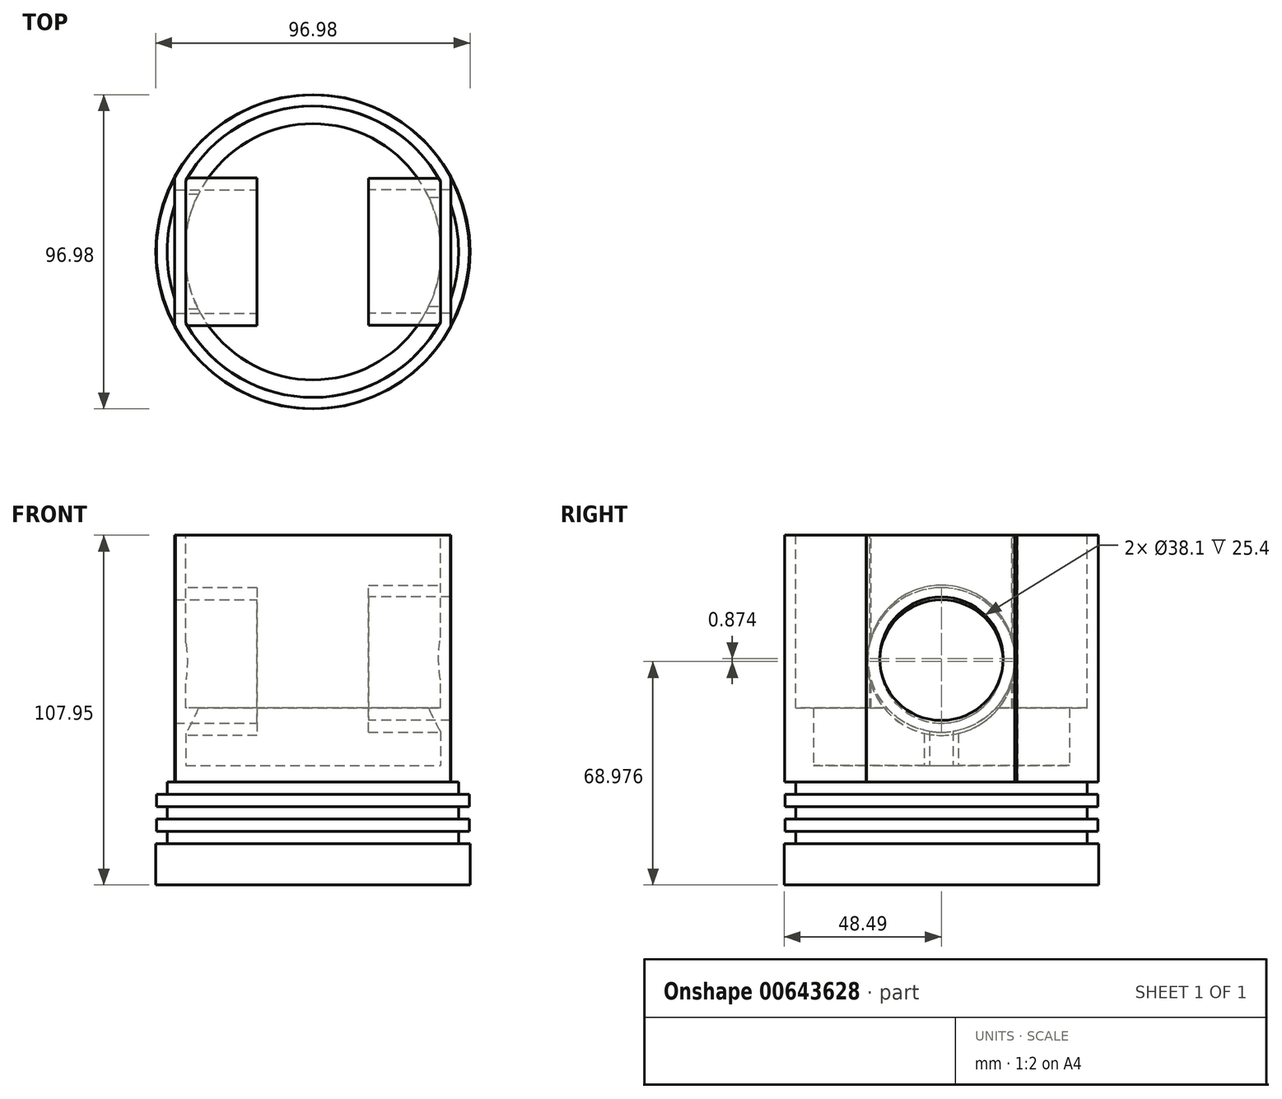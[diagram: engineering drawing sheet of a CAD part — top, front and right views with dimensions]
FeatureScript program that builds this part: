
annotation { "Feature Type Name" : "Feature", "Feature Type Description" : "" }
export const myFeature = defineFeature(function(context is Context, id is Id, definition is map)
    precondition{}
    {
        {
            var Q0;
            Q0=qCreatedBy(makeId("Top.planeOp"),FACE);
            var sketch = newSketch(context, id + "F0", { "sketchPlane" : qUnion([Q0])});
            skCircle(sketch, "E0", {"center": v(0, 0) * mm, "radius": 48.42 * mm});
            skSolve(sketch);
        }
        {
            var Q0;
            Q0=makeQuery(id+"F0.imprint","IMPRINT",FACE,{"disambiguationData":[TD([[makeQuery(id+"F0.imprint","IMPRINT",EDGE,{"derivedFrom":sQuery(id+"F0.wireOp",EDGE,"E0")}),1.0]])]});
            extrude(context, id + "F1", {"entities" : qUnion([Q0]), "depth" : 76.2 * mm, "offsetDistance" : 25.4 * mm});
        }
        {
            var Q0;
            Q0=makeQuery(id+"F1.opExtrude","CAP_FACE",FACE,{"disambiguationData":[OSD([sQuery(id+"F0.wireOp",EDGE,"E0")])],"isStart":false});
            var sketch = newSketch(context, id + "F2", { "sketchPlane" : qUnion([Q0])});
            skCircle(sketch, "E1", {"center": v(0, 0) * mm, "radius": 44.96 * mm});
            skSolve(sketch);
        }
        {
            var Q0;
            Q0=makeQuery(id+"F2.imprint","IMPRINT",FACE,{"disambiguationData":[TD([[makeQuery(id+"F2.imprint","IMPRINT",EDGE,{"derivedFrom":sQuery(id+"F2.wireOp",EDGE,"E1")}),1.0]])]});
            extrude(context, id + "F3", {"entities" : qUnion([Q0]), "operationType" : NewBodyOperationType.REMOVE, "oppositeDirection" : true, "depth" : 71.12 * mm, "offsetDistance" : 25.4 * mm});
        }
        {
            var Q0;
            Q0=qCreatedBy(makeId("Top.planeOp"),FACE);
            var sketch = newSketch(context, id + "F4", { "sketchPlane" : qUnion([Q0])});
            skCircle(sketch, "E2", {"center": v(0, 0) * mm, "radius": 44.96 * mm});
            skSolve(sketch);
        }
        {
            var Q0;
            Q0=makeQuery(id+"F4.imprint","IMPRINT",FACE,{"disambiguationData":[TD([[makeQuery(id+"F4.imprint","IMPRINT",EDGE,{"derivedFrom":sQuery(id+"F4.wireOp",EDGE,"E2")}),1.0]])]});
            extrude(context, id + "F5", {"entities" : qUnion([Q0]), "operationType" : NewBodyOperationType.ADD, "oppositeDirection" : true, "depth" : 3.8 * mm, "offsetDistance" : 25.4 * mm});
        }
        {
            var Q0;
            Q0=makeQuery(id+"F5.opExtrude","CAP_FACE",FACE,{"disambiguationData":[OSD([sQuery(id+"F4.wireOp",EDGE,"E2")])],"isStart":false});
            var sketch = newSketch(context, id + "F6", { "sketchPlane" : qUnion([Q0])});
            skCircle(sketch, "E3", {"center": v(0, 0) * mm, "radius": 48.26 * mm});
            skSolve(sketch);
        }
        {
            var Q0;
            Q0 = qSketchRegion(id + "F6", true);
            extrude(context, id + "F7", {"entities" : qUnion([Q0]), "operationType" : NewBodyOperationType.ADD, "depth" : 3.8 * mm, "offsetDistance" : 25.4 * mm});
        }
        {
            var Q0;
            Q0=makeQuery(id+"F7.opExtrude","CAP_FACE",FACE,{"disambiguationData":[OSD([sQuery(id+"F6.wireOp",EDGE,"E3")])],"isStart":false});
            var sketch = newSketch(context, id + "F8", { "sketchPlane" : qUnion([Q0])});
            skCircle(sketch, "E4", {"center": v(0, 0) * mm, "radius": 44.96 * mm});
            skSolve(sketch);
        }
        {
            var Q0;
            Q0=makeQuery(id+"F8.imprint","IMPRINT",FACE,{"disambiguationData":[TD([[makeQuery(id+"F8.imprint","IMPRINT",EDGE,{"derivedFrom":sQuery(id+"F8.wireOp",EDGE,"E4")}),1.0]])]});
            extrude(context, id + "F9", {"entities" : qUnion([Q0]), "operationType" : NewBodyOperationType.ADD, "depth" : 3.8 * mm, "offsetDistance" : 25.4 * mm});
        }
        {
            var Q0;
            Q0=makeQuery(id+"F9.opExtrude","CAP_FACE",FACE,{"disambiguationData":[OSD([sQuery(id+"F8.wireOp",EDGE,"E4")])],"isStart":false});
            var sketch = newSketch(context, id + "F10", { "sketchPlane" : qUnion([Q0])});
            skCircle(sketch, "E5", {"center": v(0, 0) * mm, "radius": 48.26 * mm});
            skSolve(sketch);
        }
        {
            var Q0;
            Q0 = qSketchRegion(id + "F10", true);
            extrude(context, id + "F11", {"entities" : qUnion([Q0]), "operationType" : NewBodyOperationType.ADD, "depth" : 3.8 * mm, "offsetDistance" : 25.4 * mm});
        }
        {
            var Q0;
            Q0=makeQuery(id+"F11.opExtrude","CAP_FACE",FACE,{"disambiguationData":[OSD([sQuery(id+"F10.wireOp",EDGE,"E5")])],"isStart":false});
            var sketch = newSketch(context, id + "F12", { "sketchPlane" : qUnion([Q0])});
            skCircle(sketch, "E6", {"center": v(0, 0) * mm, "radius": 44.96 * mm});
            skSolve(sketch);
        }
        {
            var Q0;
            Q0 = qSketchRegion(id + "F12", true);
            extrude(context, id + "F13", {"entities" : qUnion([Q0]), "operationType" : NewBodyOperationType.ADD, "depth" : 3.8 * mm, "offsetDistance" : 25.4 * mm});
        }
        {
            var Q0;
            Q0=makeQuery(id+"F13.opExtrude","CAP_FACE",FACE,{"disambiguationData":[OSD([sQuery(id+"F12.wireOp",EDGE,"E6")])],"isStart":false});
            var sketch = newSketch(context, id + "F14", { "sketchPlane" : qUnion([Q0])});
            skCircle(sketch, "E7", {"center": v(0, 0) * mm, "radius": 48.49 * mm});
            skSolve(sketch);
        }
        {
            var Q0;
            Q0 = qSketchRegion(id + "F14", true);
            extrude(context, id + "F15", {"entities" : qUnion([Q0]), "operationType" : NewBodyOperationType.ADD, "depth" : 12.7 * mm, "offsetDistance" : 25.4 * mm});
        }
        {
            var Q0;
            Q0=makeQuery(id+"F3.boolean.opBoolean","COPY",FACE,{"derivedFrom":makeQuery(id+"F3.opExtrude","CAP_FACE",FACE,{"disambiguationData":[OSD([sQuery(id+"F2.wireOp",EDGE,"E1")])],"isStart":false})});
            var sketch = newSketch(context, id + "F16", { "sketchPlane" : qUnion([Q0])});
            skCircle(sketch, "E8", {"center": v(0, 0) * mm, "radius": 39.53 * mm});
            skSolve(sketch);
        }
        {
            var Q0;
            Q0=makeQuery(id+"F16.imprint","IMPRINT",FACE,{"disambiguationData":[TD([[makeQuery(id+"F16.imprint","IMPRINT",EDGE,{"derivedFrom":sQuery(id+"F16.wireOp",EDGE,"E8")}),-1.0]])]});
            extrude(context, id + "F17", {"entities" : qUnion([Q0]), "operationType" : NewBodyOperationType.ADD, "depth" : 17.78 * mm, "offsetDistance" : 25.4 * mm});
        }
        {
            var Q0;
            Q0=qCreatedBy(makeId("Top.planeOp"),FACE);
            var sketch = newSketch(context, id + "F18", { "sketchPlane" : qUnion([Q0])});
            skLineSegment(sketch, "E9.bottom", {"start": v(-67.21, 36.5) * mm, "end": v(-42.35, 36.5) * mm});
            skLineSegment(sketch, "E9.top", {"start": v(-67.21, -44.54) * mm, "end": v(-42.35, -44.54) * mm});
            skLineSegment(sketch, "E9.left", {"start": v(-67.21, 36.5) * mm, "end": v(-67.21, -44.54) * mm});
            skLineSegment(sketch, "E9.right", {"start": v(-42.35, 36.5) * mm, "end": v(-42.35, -44.54) * mm});
            skSolve(sketch);
        }
        {
            var Q0;
            Q0=makeQuery(id+"F18.imprint","IMPRINT",FACE,{"disambiguationData":[TD([[makeQuery(id+"F18.imprint","IMPRINT",EDGE,{"derivedFrom":sQuery(id+"F18.wireOp",EDGE,"E9.bottom")}),-1.0]])]});
            extrude(context, id + "F19", {"entities" : qUnion([Q0]), "operationType" : NewBodyOperationType.REMOVE, "endBound" : BoundingType.THROUGH_ALL, "depth" : 25.4 * mm, "offsetDistance" : 25.4 * mm});
        }
        {
            var Q0;
            Q0=qCreatedBy(makeId("Top.planeOp"),FACE);
            var sketch = newSketch(context, id + "F20", { "sketchPlane" : qUnion([Q0])});
            skLineSegment(sketch, "E10.bottom", {"start": v(71.16, 37.66) * mm, "end": v(42.5, 37.66) * mm});
            skLineSegment(sketch, "E10.top", {"start": v(71.16, -45.42) * mm, "end": v(42.5, -45.42) * mm});
            skLineSegment(sketch, "E10.left", {"start": v(71.16, 37.66) * mm, "end": v(71.16, -45.42) * mm});
            skLineSegment(sketch, "E10.right", {"start": v(42.5, 37.66) * mm, "end": v(42.5, -45.42) * mm});
            skSolve(sketch);
        }
        {
            var Q0;
            Q0=makeQuery(id+"F20.imprint","IMPRINT",FACE,{"disambiguationData":[TD([[makeQuery(id+"F20.imprint","IMPRINT",EDGE,{"derivedFrom":sQuery(id+"F20.wireOp",EDGE,"E10.bottom")}),1.0]])]});
            extrude(context, id + "F21", {"entities" : qUnion([Q0]), "operationType" : NewBodyOperationType.REMOVE, "endBound" : BoundingType.THROUGH_ALL, "depth" : 25.4 * mm, "offsetDistance" : 25.4 * mm});
        }
        {
            var Q0;
            Q0=qCreatedBy(makeId("Top.planeOp"),FACE);
            var sketch = newSketch(context, id + "F22", { "sketchPlane" : qUnion([Q0])});
            skLineSegment(sketch, "E11.bottom", {"start": v(-42.59, 22.93) * mm, "end": v(-39.18, 22.93) * mm});
            skLineSegment(sketch, "E11.top", {"start": v(-42.59, -22.79) * mm, "end": v(-39.18, -22.79) * mm});
            skLineSegment(sketch, "E11.left", {"start": v(-42.59, 22.93) * mm, "end": v(-42.59, -22.79) * mm});
            skLineSegment(sketch, "E11.right", {"start": v(-39.18, 22.93) * mm, "end": v(-39.18, -22.79) * mm});
            skSolve(sketch);
        }
        {
            var Q0;
            Q0 = qSketchRegion(id + "F22", true);
            extrude(context, id + "F23", {"entities" : qUnion([Q0]), "operationType" : NewBodyOperationType.ADD, "depth" : 76.2 * mm, "offsetDistance" : 25.4 * mm});
        }
        {
            var Q0;
            Q0=qCreatedBy(makeId("Top.planeOp"),FACE);
            var sketch = newSketch(context, id + "F24", { "sketchPlane" : qUnion([Q0])});
            skLineSegment(sketch, "E12.bottom", {"start": v(42.53, 22.64) * mm, "end": v(39.36, 22.64) * mm});
            skLineSegment(sketch, "E12.top", {"start": v(42.53, -23.08) * mm, "end": v(39.36, -23.08) * mm});
            skLineSegment(sketch, "E12.left", {"start": v(42.53, 22.64) * mm, "end": v(42.53, -23.08) * mm});
            skLineSegment(sketch, "E12.right", {"start": v(39.36, 22.64) * mm, "end": v(39.36, -23.08) * mm});
            skSolve(sketch);
        }
        {
            var Q0;
            Q0 = qSketchRegion(id + "F24", true);
            extrude(context, id + "F25", {"entities" : qUnion([Q0]), "operationType" : NewBodyOperationType.ADD, "depth" : 76.2 * mm, "offsetDistance" : 25.4 * mm});
        }
        {
            var Q0;
            Q0=makeQuery(id+"F23.opExtrude","SWEPT_FACE",FACE,{"disambiguationData":[OSD([sQuery(id+"F22.wireOp",EDGE,"E11.left")])]});
            var sketch = newSketch(context, id + "F26", { "sketchPlane" : qUnion([Q0])});
            skCircle(sketch, "E13", {"center": v(0, 37.23) * mm, "radius": 22.79 * mm});
            skSolve(sketch);
        }
        {
            var Q0;
            Q0=makeQuery(id+"F26.imprint","IMPRINT",FACE,{"disambiguationData":[TD([[makeQuery(id+"F26.imprint","IMPRINT",EDGE,{"derivedFrom":sQuery(id+"F26.wireOp",EDGE,"E13")}),1.0]])]});
            extrude(context, id + "F27", {"entities" : qUnion([Q0]), "operationType" : NewBodyOperationType.ADD, "oppositeDirection" : true, "depth" : 25.4 * mm, "offsetDistance" : 25.4 * mm});
        }
        {
            var Q0;
            Q0=makeQuery(id+"F27.opExtrude","CAP_FACE",FACE,{"disambiguationData":[OSD([sQuery(id+"F26.wireOp",EDGE,"E13")])],"isStart":false});
            var sketch = newSketch(context, id + "F28", { "sketchPlane" : qUnion([Q0])});
            skCircle(sketch, "E14", {"center": v(0, 37.23) * mm, "radius": 19.05 * mm});
            skSolve(sketch);
        }
        {
            var Q0;
            Q0 = qSketchRegion(id + "F28", true);
            extrude(context, id + "F29", {"entities" : qUnion([Q0]), "operationType" : NewBodyOperationType.REMOVE, "oppositeDirection" : true, "depth" : 25.4 * mm, "offsetDistance" : 25.4 * mm});
        }
        {
            var Q0;
            Q0=makeQuery(id+"F25.opExtrude","SWEPT_FACE",FACE,{"disambiguationData":[OSD([sQuery(id+"F24.wireOp",EDGE,"E12.left")])]});
            var sketch = newSketch(context, id + "F30", { "sketchPlane" : qUnion([Q0])});
            skCircle(sketch, "E15", {"center": v(0, 38.1) * mm, "radius": 22.68 * mm});
            skSolve(sketch);
        }
        {
            var Q0;
            Q0=makeQuery(id+"F30.imprint","IMPRINT",FACE,{"disambiguationData":[TD([[makeQuery(id+"F30.imprint","IMPRINT",EDGE,{"derivedFrom":sQuery(id+"F30.wireOp",EDGE,"E15")}),1.0]])]});
            extrude(context, id + "F31", {"entities" : qUnion([Q0]), "operationType" : NewBodyOperationType.ADD, "oppositeDirection" : true, "depth" : 25.4 * mm, "offsetDistance" : 25.4 * mm});
        }
        {
            var Q0;
            Q0=makeQuery(id+"F31.opExtrude","CAP_FACE",FACE,{"disambiguationData":[OSD([sQuery(id+"F30.wireOp",EDGE,"E15")])],"isStart":false});
            var sketch = newSketch(context, id + "F32", { "sketchPlane" : qUnion([Q0])});
            skCircle(sketch, "E16", {"center": v(0, 38.1) * mm, "radius": 19.05 * mm});
            skSolve(sketch);
        }
        {
            var Q0;
            Q0=makeQuery(id+"F32.imprint","IMPRINT",FACE,{"disambiguationData":[TD([[makeQuery(id+"F32.imprint","IMPRINT",EDGE,{"derivedFrom":sQuery(id+"F32.wireOp",EDGE,"E16")}),1.0]])]});
            extrude(context, id + "F33", {"entities" : qUnion([Q0]), "operationType" : NewBodyOperationType.REMOVE, "oppositeDirection" : true, "depth" : 25.4 * mm, "offsetDistance" : 25.4 * mm});
        }
    });
